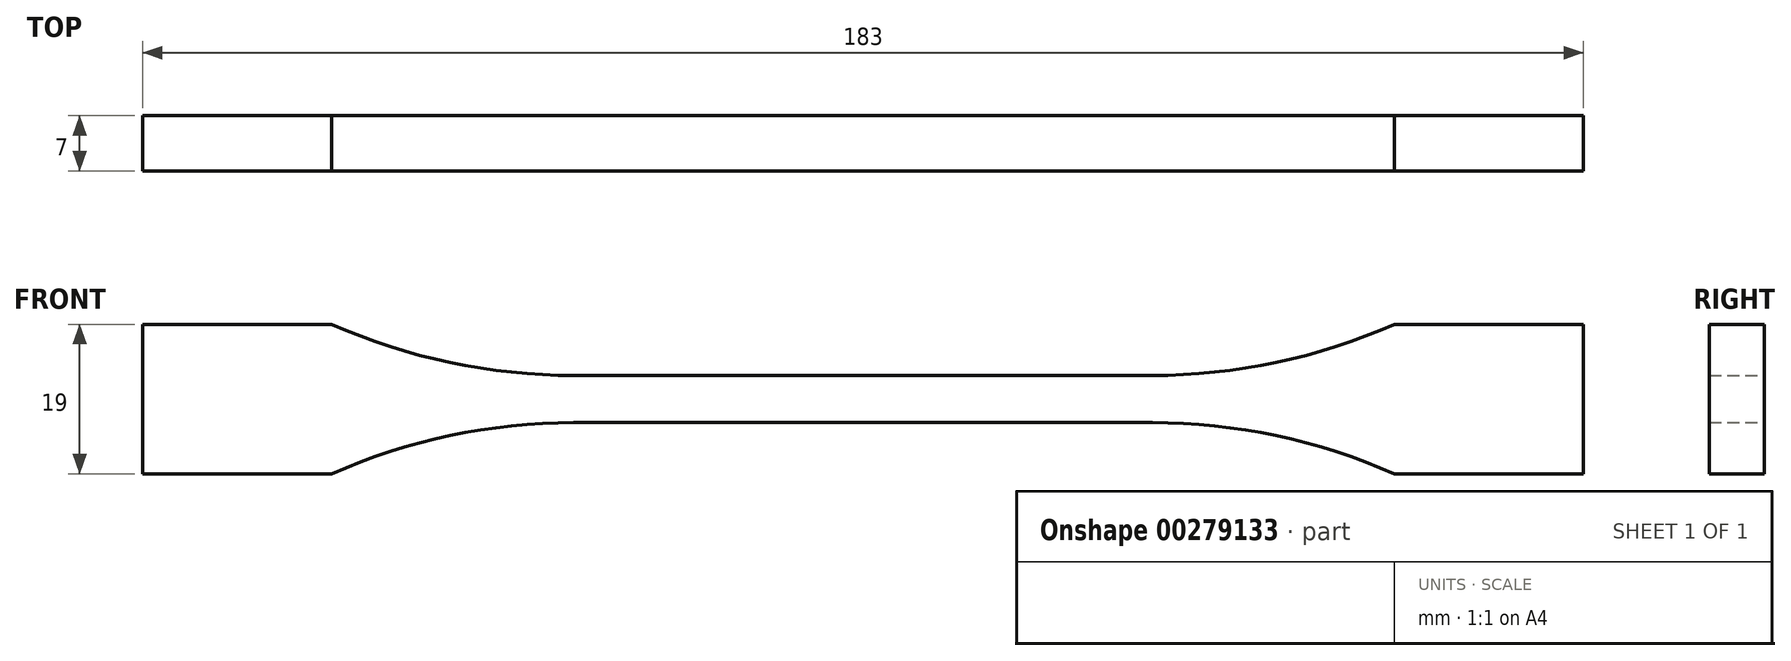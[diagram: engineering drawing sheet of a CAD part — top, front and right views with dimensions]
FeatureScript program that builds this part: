
annotation { "Feature Type Name" : "Feature", "Feature Type Description" : "" }
export const myFeature = defineFeature(function(context is Context, id is Id, definition is map)
    precondition{}
    {
        {
            var Q0;
            Q0=qCreatedBy(makeId("Front.planeOp"),FACE);
            var sketch = newSketch(context, id + "F0", { "sketchPlane" : qUnion([Q0])});
            skLineSegment(sketch, "E0", {"start": v(0, 3) * mm, "end": v(36.75, 3) * mm});
            skArc(sketch, "E1", {"start": v(36.75, 3) * mm, "mid": v(52.46, 4.64) * mm, "end": v(67.5, 9.5) * mm});
            skLineSegment(sketch, "E2", {"start": v(67.5, 9.5) * mm, "end": v(91.5, 9.5) * mm});
            skLineSegment(sketch, "E3.MirrorCS", {"start": v(67.5, -9.5) * mm, "end": v(91.5, -9.5) * mm});
            skLineSegment(sketch, "E4.MirrorCS", {"start": v(0, -3) * mm, "end": v(36.75, -3) * mm});
            skArc(sketch, "E5.MirrorCS", {"start": v(36.75, -3) * mm, "mid": v(52.46, -4.64) * mm, "end": v(67.5, -9.5) * mm});
            skLineSegment(sketch, "E6.MirrorCS", {"start": v(0, 3) * mm, "end": v(-36.75, 3) * mm});
            skLineSegment(sketch, "E7.MirrorCS", {"start": v(0, -3) * mm, "end": v(-36.75, -3) * mm});
            skArc(sketch, "E8.MirrorCS", {"start": v(-36.75, 3) * mm, "mid": v(-52.46, 4.64) * mm, "end": v(-67.5, 9.5) * mm});
            skArc(sketch, "E9.MirrorCS", {"start": v(-36.75, -3) * mm, "mid": v(-52.46, -4.64) * mm, "end": v(-67.5, -9.5) * mm});
            skLineSegment(sketch, "E10.MirrorCS", {"start": v(-67.5, 9.5) * mm, "end": v(-91.5, 9.5) * mm});
            skLineSegment(sketch, "E11.MirrorCS", {"start": v(-67.5, -9.5) * mm, "end": v(-91.5, -9.5) * mm});
            skLineSegment(sketch, "E12", {"start": v(-91.5, 9.5) * mm, "end": v(-91.5, -9.5) * mm});
            skLineSegment(sketch, "E13", {"start": v(91.5, 9.5) * mm, "end": v(91.5, -9.5) * mm});
            skSolve(sketch);
        }
        {
            var Q0;
            Q0=makeQuery(id+"F0.imprint","IMPRINT",FACE,{"disambiguationData":[TD([[makeQuery(id+"F0.imprint","IMPRINT",EDGE,{"derivedFrom":sQuery(id+"F0.wireOp",EDGE,"E0")}),-1.0]])]});
            extrude(context, id + "F1", {"entities" : qUnion([Q0]), "endBound" : BoundingType.SYMMETRIC, "depth" : 7 * mm});
        }
    });
